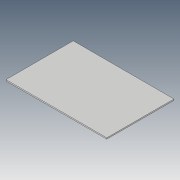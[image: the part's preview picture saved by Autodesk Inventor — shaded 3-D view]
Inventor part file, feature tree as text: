
AUTODESK INVENTOR PART (.ipt)
format: ipt  version: 2019 (Build 230136000, 136)  size: 73,728 bytes
history: native  units: mm
features: extrude x1, sketch x1
ambient origin geometry x8: Origin, YZ Plane, XZ Plane, XY Plane, X Axis, Y Axis, Z Axis, Center Point
bodies: Solid1 (feature_tree)
feature tree (2):
  extrude  "Extrusion1"  Depth=33.0mm
  sketch  "Sketch1"  dims[d0=22.0mm d1=33.0mm d2=0.4mm d3=0.0mm]
